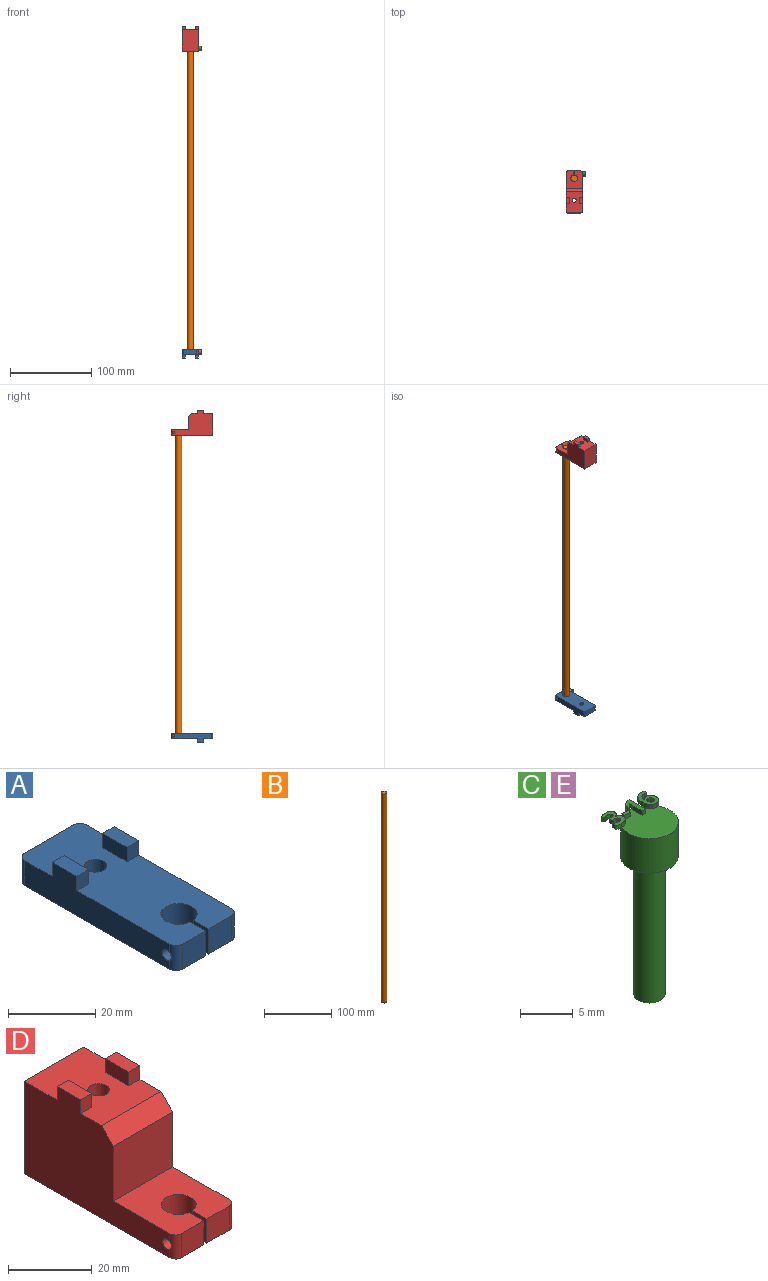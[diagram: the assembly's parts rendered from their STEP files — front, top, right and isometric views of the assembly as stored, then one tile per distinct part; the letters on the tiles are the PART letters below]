
ASSEMBLY  parts=5 mates=4
PART A: 25 faces, bbox 20x51x11 mm
  f0: plane 51x20mm, normal (0,0,1), area 877.9mm2, adj f1,f2,f3,f4,f5,f6,f7,f8
  f1: plane 16x7mm, normal (0,1,0), area 112mm2, adj f0,f10,f21,f24
  f2: plane 47x11mm, normal (-1,0,0), area 354.8mm2, adj f0,f10,f11,f13,f14,f20,f21,f22
  f3: plane 7.5x7mm, normal (0,-1,0), area 52.5mm2, adj f0,f4,f10,f22
  f4: plane 7x4.88mm, normal (1,0,0), area 27.6mm2, adj f0,f3,f5,f10,f20
  f5: cylinder r=4.15mm len=8.3mm, axis (0,0,-1), area 175.5mm2, adj f0,f4,f6,f10
  f6: plane 7x4.88mm, normal (-1,0,0), area 27.6mm2, adj f0,f5,f7,f10,f19
  f7: plane 7.5x7mm, normal (0,-1,0), area 52.5mm2, adj f0,f6,f10,f23
  f8: plane 47x11mm, normal (1,0,0), area 354.8mm2, adj f0,f10,f15,f16,f18,f19,f23,f24
  f9: cylinder r=2.55mm len=7mm, axis (0,0,-1), area 112.2mm2, adj f0,f10
  f10: plane 51x20mm, normal (0,0,-1), area 937.2mm2, adj f1,f2,f3,f4,f5,f6,f7,f8
  f11: plane 4x3.75mm, normal (0,-1,0), area 15mm2, adj f0,f2,f12,f14
  f12: plane 7.9x4mm, normal (1,0,0), area 31.6mm2, adj f0,f11,f13,f14
  f13: plane 4x3.75mm, normal (0,1,0), area 15mm2, adj f0,f2,f12,f14
  f14: plane 7.9x3.75mm, normal (0,0,1), area 29.6mm2, adj f2,f11,f12,f13
  f15: plane 4x3.75mm, normal (0,-1,0), area 15mm2, adj f0,f8,f17,f18
  f16: plane 4x3.75mm, normal (0,1,0), area 15mm2, adj f0,f8,f17,f18
  f17: plane 7.9x4mm, normal (-1,0,0), area 31.6mm2, adj f0,f15,f16,f18
  f18: plane 7.9x3.75mm, normal (0,0,1), area 29.6mm2, adj f8,f15,f16,f17
  f19: cylinder r=1.45mm len=9.5mm, axis (1,0,0), area 86.5mm2, adj f6,f8,f23
  f20: cylinder r=1.45mm len=9.5mm, axis (1,0,0), area 86.5mm2, adj f2,f4,f22
  f21: cylinder r=2mm len=7mm, axis (0,0,-1), area 22mm2, adj f0,f1,f2,f10
  f22: cylinder r=2mm len=7mm, axis (0,0,1), area 21.2mm2, adj f0,f2,f3,f10,f20
  f23: cylinder r=2mm len=7mm, axis (0,0,-1), area 21.2mm2, adj f0,f7,f8,f10,f19
  f24: cylinder r=2mm len=7mm, axis (0,0,1), area 22mm2, adj f0,f1,f8,f10
PART B: 3 faces, bbox 8x8x380 mm
  f0: cylinder r=4mm len=380mm, axis (0,0,-1), area 9550.4mm2, adj f1,f2
  f1: plane 8x8mm, normal (0,0,1), area 50.3mm2, adj f0
  f2: plane 8x8mm, normal (0,0,-1), area 50.3mm2, adj f0
PART C: 79 faces, bbox 6x6.3x20.5 mm
  f0: plane 0.44x0.4mm, normal (0,0,1), area 0.1mm2, adj f2,f68,f69,f70,f71
  f1: plane 5.5x5.5mm, normal (0,0,1), area 21.8mm2, adj f2,f28,f29,f30,f35,f36,f37,f38
  f2: cylinder r=2.75mm len=5.5mm, axis (0,0,-1), area 69.1mm2, adj f0,f1,f3,f6,f51,f78
  f3: plane 5.5x5.5mm, normal (0,0,-1), area 16.7mm2, adj f2,f4
  f4: cylinder r=1.5mm len=16mm, axis (0,0,1), area 150.8mm2, adj f3,f5
  f5: plane 3x3mm, normal (0,0,-1), area 7.1mm2, adj f4
  f6: plane 2.26x1.46mm, normal (0,0,-1), area 1.5mm2, adj f2,f7,f8,f9,f10,f11,f12,f13
  f7: extruded ~0.5x0.35mm, area 0.2mm2, adj f6,f8,f33,f34
  f8: extruded ~0.5x0.38mm, area 0.2mm2, adj f6,f7,f9,f34
  f9: extruded ~0.54x0.5mm, area 0.3mm2, adj f6,f8,f10,f34
  f10: extruded ~0.72x0.5mm, area 0.4mm2, adj f6,f9,f11,f34
  f11: plane 0.5x0.32mm, normal (-0.83,-0.56,0), area 0.2mm2, adj f6,f10,f12,f34
  f12: extruded ~0.5x0.25mm, area 0.1mm2, adj f6,f11,f13,f34
  f13: extruded ~0.5x0.22mm, area 0.1mm2, adj f6,f12,f14,f34
  f14: extruded ~0.5x0.31mm, area 0.2mm2, adj f6,f13,f15,f34
  f15: extruded ~0.5x0.23mm, area 0.1mm2, adj f6,f14,f16,f34
  f16: extruded ~0.5x0.37mm, area 0.2mm2, adj f6,f15,f17,f34
  f17: plane 0.5x0.17mm, normal (0,1,0), area 0.1mm2, adj f6,f16,f18,f34
  f18: plane 0.5x0.36mm, normal (-1,0,0), area 0.2mm2, adj f6,f17,f19,f34
  f19: plane 0.5x0.17mm, normal (0,-1,0), area 0.1mm2, adj f6,f18,f20,f34
  f20: extruded ~0.5x0.4mm, area 0.2mm2, adj f6,f19,f21,f34
  f21: extruded ~0.5x0.22mm, area 0.1mm2, adj f6,f20,f22,f34
  f22: extruded ~0.5x0.25mm, area 0.1mm2, adj f6,f21,f23,f34
  f23: extruded ~0.5x0.34mm, area 0.2mm2, adj f6,f22,f24,f34
  f24: extruded ~0.5x0.3mm, area 0.2mm2, adj f6,f23,f25,f34
  f25: extruded ~0.5x0.28mm, area 0.2mm2, adj f6,f24,f26,f34
  f26: plane 0.5x0.4mm, normal (-1,0,0), area 0.2mm2, adj f6,f25,f27,f34
  f27: extruded ~0.63x0.5mm, area 0.3mm2, adj f6,f26,f28,f34
  f28: extruded ~0.66x0.5mm, area 0.3mm2, adj f1,f6,f27,f29,f34
  f29: extruded ~0.5x0.49mm, area 0.3mm2, adj f1,f28,f30,f34
  f30: extruded ~0.5x0.35mm, area 0.2mm2, adj f1,f6,f29,f31,f34
  f31: extruded ~0.5x0.4mm, area 0.2mm2, adj f6,f30,f32,f34
  f32: plane 0.5x0.01mm, normal (1,0,0), area 0mm2, adj f6,f31,f33,f34
  f33: extruded ~0.5x0.35mm, area 0.2mm2, adj f6,f7,f32,f34
  f34: plane 2.26x1.52mm, normal (0,0,1), area 1.8mm2, adj f7,f8,f9,f10,f11,f12,f13,f14
  f35: plane 0.5x0.38mm, normal (-1,0,0), area 0.2mm2, adj f1,f36,f38,f39
  f36: plane 0.81x0.5mm, normal (0,-1,0), area 0.4mm2, adj f1,f35,f37,f39
  f37: plane 0.5x0.38mm, normal (1,0,0), area 0.2mm2, adj f1,f36,f38,f39
  f38: plane 0.81x0.5mm, normal (0,1,0), area 0.4mm2, adj f1,f35,f37,f39
  f39: plane 0.81x0.38mm, normal (0,0,1), area 0.3mm2, adj f35,f36,f37,f38
  f40: plane 0.5x0.46mm, normal (0,-1,0), area 0.2mm2, adj f1,f41,f49,f50
  f41: plane 2.2x0.5mm, normal (1,0,0), area 1.1mm2, adj f1,f40,f42,f50,f51
  f42: plane 0.5x0.38mm, normal (0,1,0), area 0.2mm2, adj f41,f43,f50,f51
  f43: plane 0.71x0.56mm, normal (-0.62,0.78,0), area 0.5mm2, adj f42,f44,f50,f51
  f44: plane 0.5x0.28mm, normal (-0.78,-0.63,0), area 0.2mm2, adj f1,f43,f45,f50,f51
  f45: plane 0.5x0.25mm, normal (0.63,-0.78,0), area 0.2mm2, adj f1,f44,f46,f50,f51
  f46: extruded ~0.5x0.16mm, area 0.1mm2, adj f45,f47,f50,f51
  f47: plane 0.5x0.23mm, normal (-1,0.03,0), area 0.1mm2, adj f46,f48,f50,f51
  f48: plane 0.5x0.21mm, normal (-1,0.02,0), area 0.1mm2, adj f1,f47,f49,f50,f51
  f49: plane 1.27x0.5mm, normal (-1,0,0), area 0.6mm2, adj f1,f40,f48,f50
  f50: plane 2.2x1.09mm, normal (0,0,1), area 1.2mm2, adj f40,f41,f42,f43,f44,f45,f46,f47
  f51: plane 1.09x0.84mm, normal (0,0,-1), area 0.6mm2, adj f2,f41,f42,f43,f44,f45,f46,f47
  f52: extruded ~0.97x0.5mm, area 0.5mm2, adj f1,f53,f76,f77,f78
  f53: extruded ~0.52x0.5mm, area 0.3mm2, adj f1,f52,f54,f77
  f54: extruded ~0.5x0.33mm, area 0.2mm2, adj f1,f53,f55,f77
  f55: extruded ~0.5x0.42mm, area 0.2mm2, adj f1,f54,f56,f77
  f56: extruded ~0.55x0.5mm, area 0.3mm2, adj f1,f55,f57,f77,f78
  f57: extruded ~0.56x0.5mm, area 0.3mm2, adj f56,f58,f77,f78
  f58: extruded ~0.51x0.5mm, area 0.3mm2, adj f57,f59,f77,f78
  f59: extruded ~0.5x0.46mm, area 0.3mm2, adj f58,f60,f77,f78
  f60: extruded ~0.5x0.48mm, area 0.3mm2, adj f59,f61,f77,f78
  f61: plane 0.5x0.02mm, normal (0,1,0), area 0mm2, adj f60,f62,f77,f78
  f62: extruded ~0.5x0.4mm, area 0.2mm2, adj f61,f63,f77,f78
  f63: extruded ~0.5x0.23mm, area 0.2mm2, adj f62,f64,f77,f78
  f64: extruded ~0.5x0.39mm, area 0.2mm2, adj f63,f65,f77,f78
  f65: extruded ~0.5x0.26mm, area 0.1mm2, adj f64,f66,f77,f78
  f66: plane 0.5x0.37mm, normal (1,0,0), area 0.2mm2, adj f65,f67,f77,f78
  f67: extruded ~0.5x0.29mm, area 0.1mm2, adj f66,f76,f77,f78
  f68: extruded ~0.5x0.23mm, area 0.1mm2, adj f0,f69,f75,f77,f78
  f69: extruded ~0.5x0.24mm, area 0.1mm2, adj f0,f68,f70,f77
  f70: extruded ~0.5x0.3mm, area 0.2mm2, adj f0,f69,f71,f77
  f71: extruded ~0.5x0.21mm, area 0.1mm2, adj f0,f70,f72,f77,f78
  f72: extruded ~0.5x0.24mm, area 0.1mm2, adj f71,f73,f77,f78
  f73: extruded ~0.5x0.22mm, area 0.1mm2, adj f72,f74,f77,f78
  f74: extruded ~0.5x0.25mm, area 0.1mm2, adj f73,f75,f77,f78
  f75: extruded ~0.5x0.28mm, area 0.2mm2, adj f68,f74,f77,f78
  f76: extruded ~0.83x0.5mm, area 0.5mm2, adj f52,f67,f77,f78
  f77: plane 2.25x1.55mm, normal (0,0,1), area 2.1mm2, adj f52,f53,f54,f55,f56,f57,f58,f59
  f78: plane 2.22x1.55mm, normal (0,0,-1), area 1.5mm2, adj f2,f52,f56,f57,f58,f59,f60,f61
PART D: 28 faces, bbox 20x51x31 mm
  f0: cylinder r=5.5mm len=22mm, axis (0,0,-1), area 760.3mm2, adj f10,f26
  f1: plane 21x20mm, normal (0,0,1), area 359.3mm2, adj f2,f3,f4,f5,f6,f7,f8,f13
  f2: plane 49x31mm, normal (-1,0,0), area 960.8mm2, adj f1,f9,f10,f12,f13,f15,f16,f17
  f3: plane 7.5x7mm, normal (0,-1,0), area 52.5mm2, adj f1,f4,f10,f13
  f4: plane 7x4.88mm, normal (1,0,0), area 27.6mm2, adj f1,f3,f5,f10,f12
  f5: cylinder r=4.15mm len=8.3mm, axis (0,0,-1), area 175.5mm2, adj f1,f4,f6,f10
  f6: plane 7x4.88mm, normal (-1,0,0), area 27.6mm2, adj f1,f5,f7,f10,f11
  f7: plane 7.5x7mm, normal (0,-1,0), area 52.5mm2, adj f1,f6,f10,f14
  f8: plane 49x31mm, normal (1,0,0), area 960.8mm2, adj f1,f9,f10,f11,f14,f15,f16,f21
  f9: plane 27x20mm, normal (0,1,0), area 540mm2, adj f2,f8,f10,f16
  f10: plane 51x20mm, normal (0,0,-1), area 864.3mm2, adj f0,f2,f3,f4,f5,f6,f7,f8
  f11: cylinder r=1.45mm len=9.5mm, axis (1,0,0), area 86.5mm2, adj f6,f8,f14
  f12: cylinder r=1.45mm len=9.5mm, axis (1,0,0), area 86.5mm2, adj f2,f4,f13
  f13: cylinder r=2mm len=7mm, axis (0,0,1), area 21.2mm2, adj f1,f2,f3,f10,f12
  f14: cylinder r=2mm len=7mm, axis (0,0,-1), area 21.2mm2, adj f1,f7,f8,f10,f11
  f15: plane 20x16mm, normal (0,-1,0), area 320mm2, adj f1,f2,f8,f25
  f16: plane 26x20mm, normal (0,0,1), area 440.3mm2, adj f2,f8,f9,f17,f18,f19,f21,f22
  f17: plane 4x3.75mm, normal (0,1,0), area 15mm2, adj f2,f16,f18,f20
  f18: plane 7.9x4mm, normal (1,0,0), area 31.6mm2, adj f16,f17,f19,f20
  f19: plane 4x3.75mm, normal (0,-1,0), area 15mm2, adj f2,f16,f18,f20
  f20: plane 7.9x3.75mm, normal (0,0,1), area 29.6mm2, adj f2,f17,f18,f19
  f21: plane 4x3.75mm, normal (0,-1,0), area 15mm2, adj f8,f16,f22,f24
  f22: plane 7.9x4mm, normal (-1,0,0), area 31.6mm2, adj f16,f21,f23,f24
  f23: plane 4x3.75mm, normal (0,1,0), area 15mm2, adj f8,f16,f22,f24
  f24: plane 7.9x3.75mm, normal (0,0,1), area 29.6mm2, adj f8,f21,f22,f23
  f25: plane 20x4mm, normal (0,-0.71,0.71), area 113.1mm2, adj f2,f8,f15,f16
  f26: plane 11x11mm, normal (0,0,-1), area 74.6mm2, adj f0,f27
  f27: cylinder r=2.55mm len=5.1mm, axis (0,0,-1), area 80.1mm2, adj f16,f26
PART E: same geometry as C
PLACE A rot(axis=(1,0,0),180deg) t=(68.67,74.18,-172.64)mm
PLACE B t=(71.03,65.18,-179.64)mm
PLACE C rot(axis=(0.71,0,0.71),180deg) t=(81.03,71.23,186.86)mm
PLACE D rot(axis=(0,0,1),180deg) t=(74.44,74.18,193.36)mm
PLACE E rot(axis=(0.71,0,0.71),180deg) t=(81.03,71.23,-186.14)mm
MATE fastened B.f0 <-> D.f5  axis (0,0,1) through (71.03,65.18,200.36)mm
MATE fastened B.f0 <-> A.f5  axis (0,0,-1) through (71.03,65.18,-179.64)mm
MATE fastened E.f2 <-> A.f19  axis (-1,0,0) through (81.03,71.23,-176.14)mm
MATE fastened C.f2 <-> D.f11  axis (-1,0,0) through (81.03,71.23,196.86)mm
